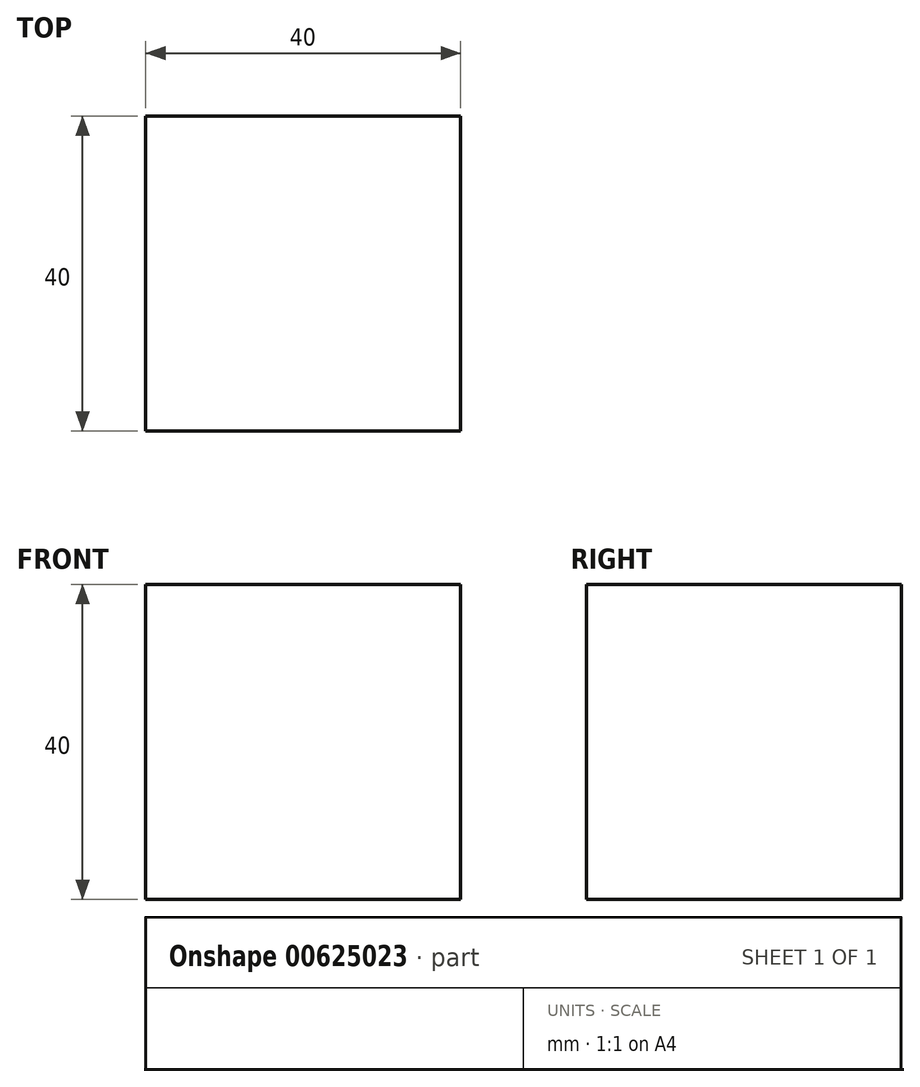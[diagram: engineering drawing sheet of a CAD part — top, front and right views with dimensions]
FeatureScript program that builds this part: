
annotation { "Feature Type Name" : "Feature", "Feature Type Description" : "" }
export const myFeature = defineFeature(function(context is Context, id is Id, definition is map)
    precondition{}
    {
        {
            var Q0;
            Q0=qCreatedBy(makeId("Top.planeOp"),FACE);
            var sketch = newSketch(context, id + "F0", { "sketchPlane" : qUnion([Q0])});
            skLineSegment(sketch, "E0.bottom", {"start": v(20, 20) * mm, "end": v(-20, 20) * mm});
            skLineSegment(sketch, "E0.top", {"start": v(20, -20) * mm, "end": v(-20, -20) * mm});
            skLineSegment(sketch, "E0.left", {"start": v(20, 20) * mm, "end": v(20, -20) * mm});
            skLineSegment(sketch, "E0.right", {"start": v(-20, 20) * mm, "end": v(-20, -20) * mm});
            skPoint(sketch, "E0.middle", {"position": v(0, 0) * mm});
            skSolve(sketch);
        }
        {
            var Q0;
            Q0 = qSketchRegion(id + "F0", true);
            extrude(context, id + "F1", {"entities" : qUnion([Q0]), "endBound" : BoundingType.SYMMETRIC, "depth" : 40 * mm, "offsetDistance" : 25 * mm});
        }
    });
